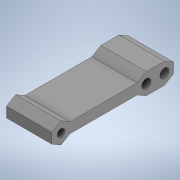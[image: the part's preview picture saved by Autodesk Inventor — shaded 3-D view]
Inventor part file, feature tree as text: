
AUTODESK INVENTOR PART (.ipt)
format: ipt  version: 2020 (Build 240168000, 168)  size: 271,360 bytes
history: native  units: in
note: dims shown in document units (in); Inventor stores cm internally (conversion verified against a paired STEP export)
features: sketch x5, extrude x4, plane x2, projected_geometry x2, mirror x1
ambient origin geometry x8: Origin, YZ Plane, XZ Plane, XY Plane, X Axis, Y Axis, Z Axis, Center Point
bodies: Solid1 (feature_tree)
feature tree (14):
  extrude  "Extrusion1"  Depth=2.1137in
  plane  "Work Plane1"
  extrude  "Extrusion2"  Depth=0.7874in
  sketch  "Sketch4"  dims[d4=0.0in d5=0.0787in]
  extrude  "Extrusion4"  Depth=0.0787in
  plane  "Work Plane2"
  extrude  "Extrusion6"  Depth=1.7988in
  mirror  "Mirror2"
  sketch  "Sketch1"  dims[d0=0.1818in d1=2.1137in]
  sketch  "Sketch2"  dims[d2=0.1299in d3=0.7874in]
  sketch  "Sketch5"  dims[d6=0.7874in d7=0.0in d28=1.7988in]
  sketch  "Sketch7"  dims[d29=0.315in d31=0.315in d33=0.1575in d34=0.2362in d35=0.0in d38=0.315in d39=0.2756in d40=-0.3092in]
  projected_geometry  "Projected Loop7"
  projected_geometry  "Projected Loop8"
